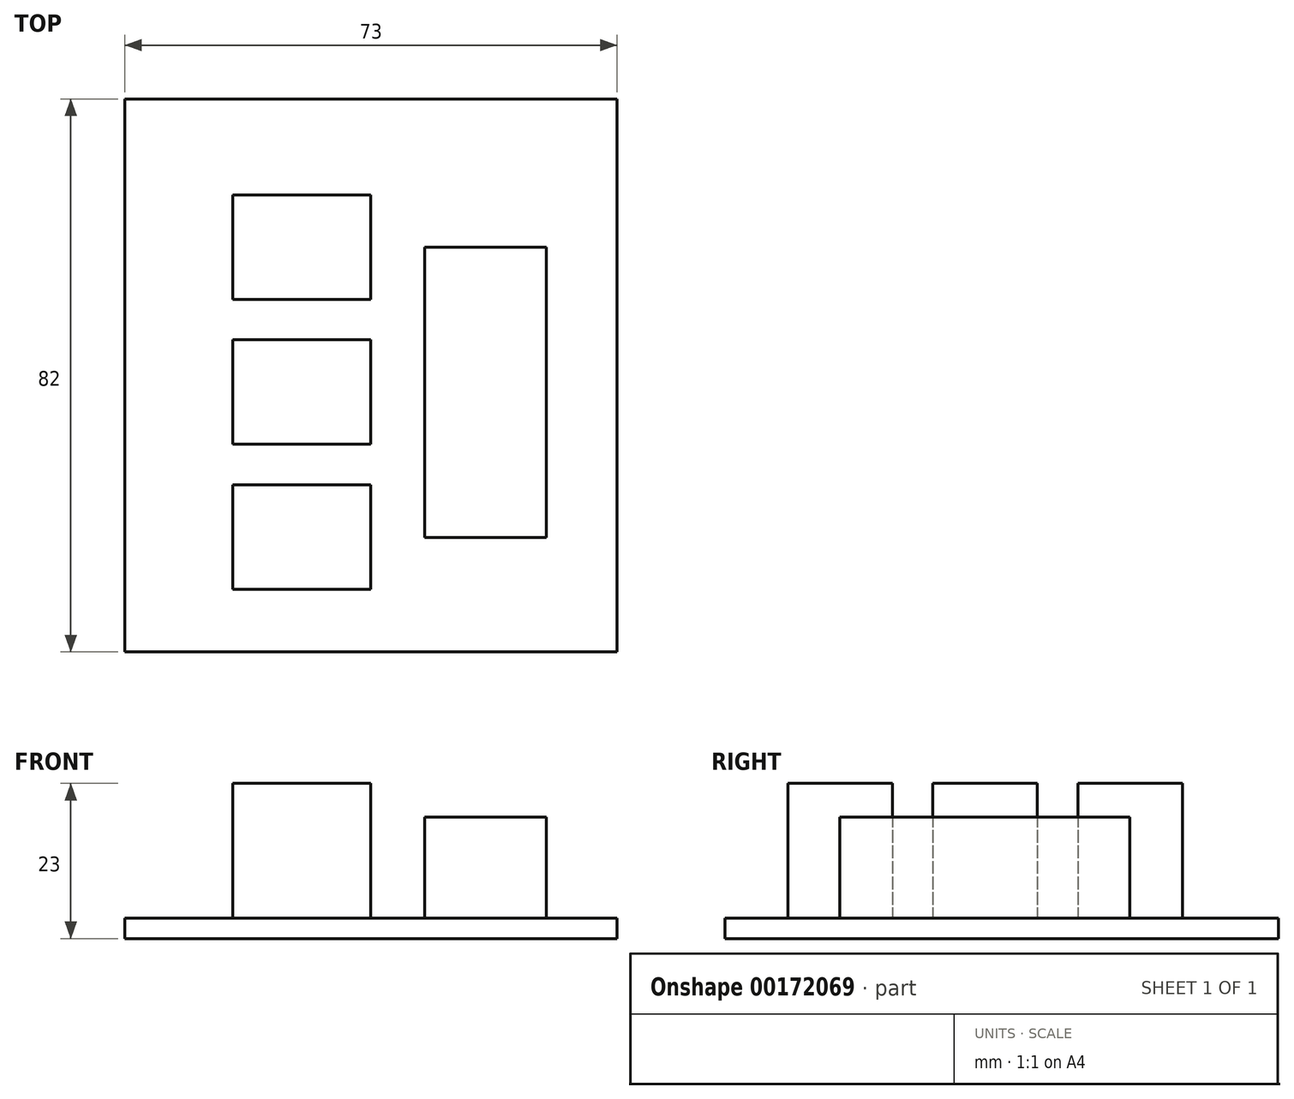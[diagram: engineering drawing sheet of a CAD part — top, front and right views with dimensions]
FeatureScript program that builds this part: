
annotation { "Feature Type Name" : "Feature", "Feature Type Description" : "" }
export const myFeature = defineFeature(function(context is Context, id is Id, definition is map)
    precondition{}
    {
        {
            var Q0;
            Q0=qCreatedBy(makeId("Top.planeOp"),FACE);
            var sketch = newSketch(context, id + "F0", { "sketchPlane" : qUnion([Q0])});
            skLineSegment(sketch, "E0.bottom", {"start": v(36.5, 41) * mm, "end": v(-36.5, 41) * mm});
            skLineSegment(sketch, "E0.top", {"start": v(36.5, -41) * mm, "end": v(-36.5, -41) * mm});
            skLineSegment(sketch, "E0.left", {"start": v(36.5, 41) * mm, "end": v(36.5, -41) * mm});
            skLineSegment(sketch, "E0.right", {"start": v(-36.5, 41) * mm, "end": v(-36.5, -41) * mm});
            skPoint(sketch, "E0.middle", {"position": v(0, 0) * mm});
            skLineSegment(sketch, "E1.bottom", {"start": v(0, 11.3) * mm, "end": v(-20.5, 11.3) * mm});
            skLineSegment(sketch, "E1.top", {"start": v(0, 26.8) * mm, "end": v(-20.5, 26.8) * mm});
            skLineSegment(sketch, "E1.left", {"start": v(0, 11.3) * mm, "end": v(0, 26.8) * mm});
            skLineSegment(sketch, "E1.right", {"start": v(-20.5, 11.3) * mm, "end": v(-20.5, 26.8) * mm});
            skPoint(sketch, "E1.middle", {"position": v(-10.25, 19.05) * mm});
            skLineSegment(sketch, "E2.bottom", {"start": v(0, -10.2) * mm, "end": v(-20.5, -10.2) * mm});
            skLineSegment(sketch, "E2.top", {"start": v(0, 5.3) * mm, "end": v(-20.5, 5.3) * mm});
            skLineSegment(sketch, "E2.left", {"start": v(0, -10.2) * mm, "end": v(0, 5.3) * mm});
            skLineSegment(sketch, "E2.right", {"start": v(-20.5, -10.2) * mm, "end": v(-20.5, 5.3) * mm});
            skPoint(sketch, "E2.middle", {"position": v(-10.25, -2.45) * mm});
            skLineSegment(sketch, "E3.bottom", {"start": v(0, -31.7) * mm, "end": v(-20.5, -31.7) * mm});
            skLineSegment(sketch, "E3.top", {"start": v(0, -16.2) * mm, "end": v(-20.5, -16.2) * mm});
            skLineSegment(sketch, "E3.left", {"start": v(0, -31.7) * mm, "end": v(0, -16.2) * mm});
            skLineSegment(sketch, "E3.right", {"start": v(-20.5, -31.7) * mm, "end": v(-20.5, -16.2) * mm});
            skPoint(sketch, "E3.middle", {"position": v(-10.25, -23.95) * mm});
            skLineSegment(sketch, "E4.bottom", {"start": v(26, 19) * mm, "end": v(8, 19) * mm});
            skLineSegment(sketch, "E4.top", {"start": v(26, -24) * mm, "end": v(8, -24) * mm});
            skLineSegment(sketch, "E4.left", {"start": v(26, 19) * mm, "end": v(26, -24) * mm});
            skLineSegment(sketch, "E4.right", {"start": v(8, 19) * mm, "end": v(8, -24) * mm});
            skPoint(sketch, "E4.middle", {"position": v(17, -2.5) * mm});
            skLineSegment(sketch, "E5", {"start": v(-10.25, -2.45) * mm, "end": v(-10.25, 19.05) * mm, "construction": true});
            skLineSegment(sketch, "E6", {"start": v(-10.25, -23.95) * mm, "end": v(-10.25, -2.45) * mm, "construction": true});
            skSolve(sketch);
        }
        {
            var Q0;
            Q0=makeQuery(id+"F0.imprint","IMPRINT",FACE,{"disambiguationData":[TD([[makeQuery(id+"F0.imprint","IMPRINT",EDGE,{"derivedFrom":sQuery(id+"F0.wireOp",EDGE,"E0.bottom")}),1.0]])]});
            var Q1;
            Q1=makeQuery(id+"F0.imprint","IMPRINT",FACE,{"disambiguationData":[TD([[makeQuery(id+"F0.imprint","IMPRINT",EDGE,{"derivedFrom":sQuery(id+"F0.wireOp",EDGE,"E4.bottom")}),1.0]])]});
            var Q2;
            Q2=makeQuery(id+"F0.imprint","IMPRINT",FACE,{"disambiguationData":[TD([[makeQuery(id+"F0.imprint","IMPRINT",EDGE,{"derivedFrom":sQuery(id+"F0.wireOp",EDGE,"E2.bottom")}),-1.0]])]});
            var Q3;
            Q3=makeQuery(id+"F0.imprint","IMPRINT",FACE,{"disambiguationData":[TD([[makeQuery(id+"F0.imprint","IMPRINT",EDGE,{"derivedFrom":sQuery(id+"F0.wireOp",EDGE,"E3.bottom")}),-1.0]])]});
            var Q4;
            Q4=makeQuery(id+"F0.imprint","IMPRINT",FACE,{"disambiguationData":[TD([[makeQuery(id+"F0.imprint","IMPRINT",EDGE,{"derivedFrom":sQuery(id+"F0.wireOp",EDGE,"E1.bottom")}),-1.0]])]});
            extrude(context, id + "F1", {"entities" : qUnion([Q0, Q1, Q2, Q3, Q4]), "oppositeDirection" : true, "depth" : 3 * mm});
        }
        {
            var Q0;
            Q0=makeQuery(id+"F0.imprint","IMPRINT",FACE,{"disambiguationData":[TD([[makeQuery(id+"F0.imprint","IMPRINT",EDGE,{"derivedFrom":sQuery(id+"F0.wireOp",EDGE,"E3.bottom")}),-1.0]])]});
            var Q1;
            Q1=makeQuery(id+"F0.imprint","IMPRINT",FACE,{"disambiguationData":[TD([[makeQuery(id+"F0.imprint","IMPRINT",EDGE,{"derivedFrom":sQuery(id+"F0.wireOp",EDGE,"E2.bottom")}),-1.0]])]});
            var Q2;
            Q2=makeQuery(id+"F0.imprint","IMPRINT",FACE,{"disambiguationData":[TD([[makeQuery(id+"F0.imprint","IMPRINT",EDGE,{"derivedFrom":sQuery(id+"F0.wireOp",EDGE,"E1.bottom")}),-1.0]])]});
            extrude(context, id + "F2", {"entities" : qUnion([Q0, Q1, Q2]), "operationType" : NewBodyOperationType.ADD, "depth" : 20 * mm});
        }
        {
            var Q0;
            Q0=makeQuery(id+"F0.imprint","IMPRINT",FACE,{"disambiguationData":[TD([[makeQuery(id+"F0.imprint","IMPRINT",EDGE,{"derivedFrom":sQuery(id+"F0.wireOp",EDGE,"E4.bottom")}),1.0]])]});
            extrude(context, id + "F3", {"entities" : qUnion([Q0]), "operationType" : NewBodyOperationType.ADD, "depth" : 15 * mm});
        }
    });
